# Revit family: Domotics-DomesticRanges-GEWISS-27COMBIIN_SYSTEM-IP55_WATERTIGHT_2M
name_source: partatom
category: Apparecchi elettrici
revit_build: Autodesk Revit 2016 (Build: 20161004_0715(x64)
units: mm (PartAtom-declared; Revit-internal decimal feet)

## family parameters
Basato su piano di lavoro = No
Condiviso = No
Mantenere orientamento annotazione = No
Numero OmniClass = 23.80.30.14.24
Punto di calcolo locali = No
Quota connettore circolare = Usa diametro
Sempre verticale = Sì
Taglio con vuoti quando caricato = No
Tipo di parte = Normale
Titolo OmniClass = Junction Boxes

## types (1)
- GW27401 - System 2 gang watertight cover
    Altezza da terra = 850 mm  [stored 2.78871 ft]
    Catalogue = DOMOTICS
    Catalogue Range = 27COMBI
    Characteristics = Halogen free
    Colour = Grey RAL 7035
    Descrizione = SYSTEM 2 GANG WATERTIGHT COVER
    Dimensions LxH (mm) = 75x85
    Door colour: = Transparent
    Door type = With membrane
    EAN code = 8011564055605
    Electrocod = 0110
    Finitura = <Per categoria>
    Glow Wire Test = 650°C
    IDF = 34a4a570-8e99-4831-a890-147d7284a0c3
    IDT = 01007444-aaaf-43a2-be93-58eade9c0c9a
    IP degree = IP55
    Immagine tipo = GW27401.jpg
    Installation temperature = -25 +60 °C
    Insulation class = II
    Larghezza = 75 mm
    Lid screws = Stainless steel
    Lunghezza = 85 mm  [stored 0.278871 ft]
    Modello = GW27401
    No. SYSTEM modules = 2
    Produttore = GEWISS S.p.A.
    Profondità = 20 mm  [stored 0.0656168 ft]
    SEO = Cap
    Shock resistance = IK07
    Standard = EN 60669-1
    Standard; = EN 60669-1
    Suitable for = 2 SYSTEM modules
    Technical sheet = https://www.gewiss.com
    Thermo-pressure with ball = 70
    Torque screws tightening = 0,8NM
    URL = https://www.gewiss.com
    Version file RFA = 19.4
    Vetro Sportello = Vetro

note: source unit labels omitted for Thermo-pressure with ball — the stored unit's dimension contradicts the parameter name (converter mislabeling)

note: [stored X ft] marks values corroborated as IEEE doubles in the binary element streams (Revit-internal decimal feet)
